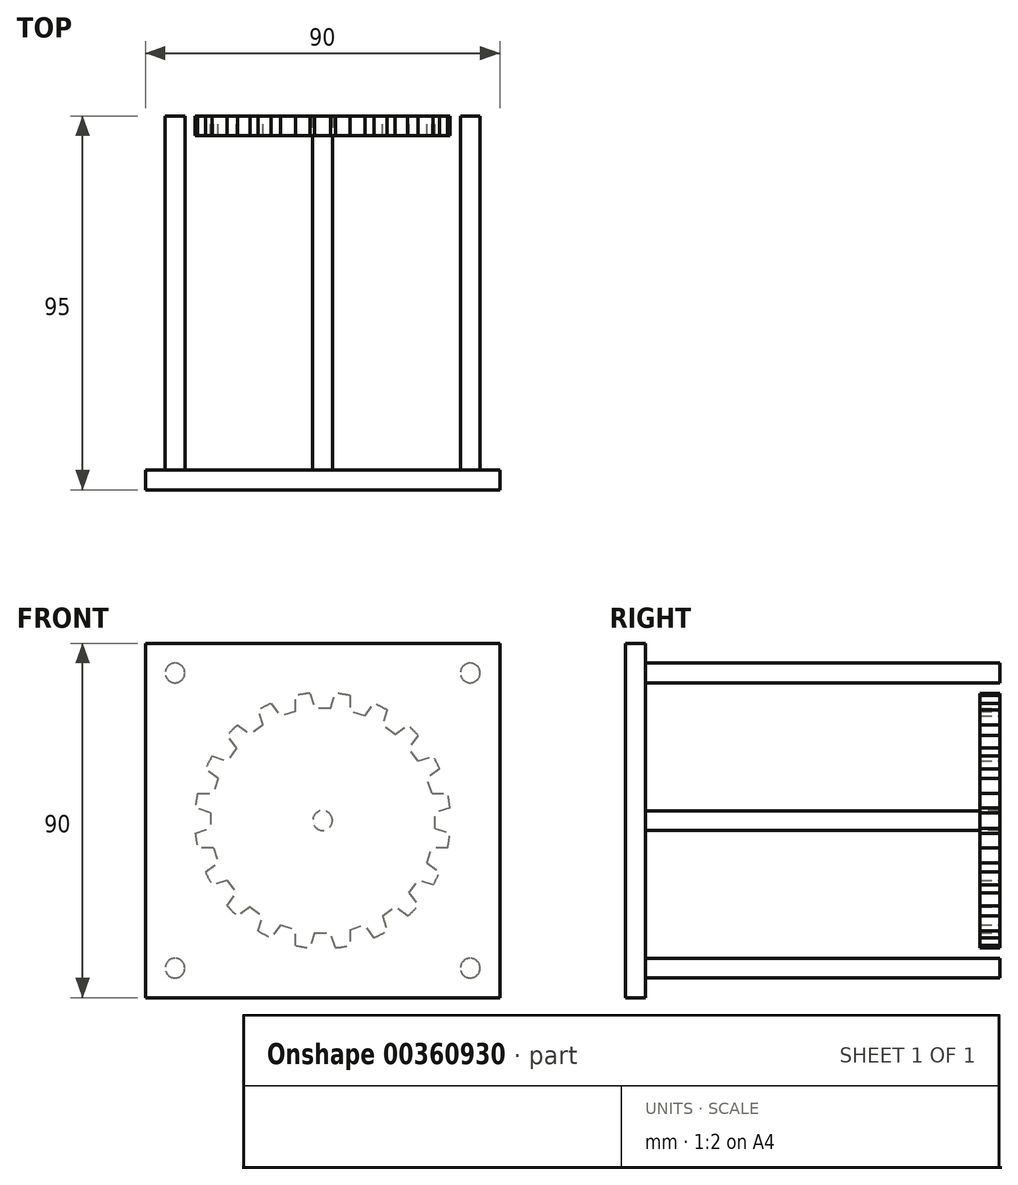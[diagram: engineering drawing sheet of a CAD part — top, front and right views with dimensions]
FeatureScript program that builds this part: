
annotation { "Feature Type Name" : "Feature", "Feature Type Description" : "" }
export const myFeature = defineFeature(function(context is Context, id is Id, definition is map)
    precondition{}
    {
        {
            var Q0;
            Q0=qCreatedBy(makeId("Front.planeOp"),FACE);
            var sketch = newSketch(context, id + "F0", { "sketchPlane" : qUnion([Q0])});
            skLineSegment(sketch, "E0.bottom", {"start": v(45, 45) * mm, "end": v(-45, 45) * mm});
            skLineSegment(sketch, "E0.top", {"start": v(45, -45) * mm, "end": v(-45, -45) * mm});
            skLineSegment(sketch, "E0.left", {"start": v(45, 45) * mm, "end": v(45, -45) * mm});
            skLineSegment(sketch, "E0.right", {"start": v(-45, 45) * mm, "end": v(-45, -45) * mm});
            skSolve(sketch);
        }
        {
            var Q0;
            Q0=makeQuery(id+"F0.imprint","IMPRINT",FACE,{"disambiguationData":[TD([[makeQuery(id+"F0.imprint","IMPRINT",EDGE,{"derivedFrom":sQuery(id+"F0.wireOp",EDGE,"E0.bottom")}),1.0]])]});
            extrude(context, id + "F1", {"entities" : qUnion([Q0]), "depth" : 5 * mm});
        }
        {
            var Q0;
            Q0=makeQuery(id+"F1.opExtrude","CAP_FACE",FACE,{"disambiguationData":[OSD([sQuery(id+"F0.wireOp",EDGE,"E0.bottom"),sQuery(id+"F0.wireOp",EDGE,"E0.top"),sQuery(id+"F0.wireOp",EDGE,"E0.left"),sQuery(id+"F0.wireOp",EDGE,"E0.right")])],"isStart":true});
            var sketch = newSketch(context, id + "F2", { "sketchPlane" : qUnion([Q0])});
            skCircle(sketch, "E1", {"center": v(0, 0) * mm, "radius": 2.5 * mm});
            skSolve(sketch);
        }
        {
            var Q0;
            Q0 = qSketchRegion(id + "F2", true);
            extrude(context, id + "F3", {"entities" : qUnion([Q0]), "operationType" : NewBodyOperationType.ADD, "depth" : 90 * mm});
        }
        {
            var Q0;
            Q0=makeQuery(id+"F1.opExtrude","CAP_FACE",FACE,{"disambiguationData":[OSD([sQuery(id+"F0.wireOp",EDGE,"E0.bottom"),sQuery(id+"F0.wireOp",EDGE,"E0.top"),sQuery(id+"F0.wireOp",EDGE,"E0.left"),sQuery(id+"F0.wireOp",EDGE,"E0.right")])],"isStart":true});
            var sketch = newSketch(context, id + "F4", { "sketchPlane" : qUnion([Q0])});
            skCircle(sketch, "E2", {"center": v(-37.5, 37.5) * mm, "radius": 2.5 * mm});
            skCircle(sketch, "E3", {"center": v(37.5, 37.5) * mm, "radius": 2.5 * mm});
            skCircle(sketch, "E4", {"center": v(37.5, -37.5) * mm, "radius": 2.5 * mm});
            skCircle(sketch, "E5", {"center": v(-37.5, -37.5) * mm, "radius": 2.5 * mm});
            skSolve(sketch);
        }
        {
            var Q0;
            Q0=makeQuery(id+"F4.imprint","IMPRINT",FACE,{"disambiguationData":[TD([[makeQuery(id+"F4.imprint","IMPRINT",EDGE,{"derivedFrom":sQuery(id+"F4.wireOp",EDGE,"E2")}),1.0]])]});
            var Q1;
            Q1=makeQuery(id+"F4.imprint","IMPRINT",FACE,{"disambiguationData":[TD([[makeQuery(id+"F4.imprint","IMPRINT",EDGE,{"derivedFrom":sQuery(id+"F4.wireOp",EDGE,"E3")}),1.0]])]});
            var Q2;
            Q2=makeQuery(id+"F4.imprint","IMPRINT",FACE,{"disambiguationData":[TD([[makeQuery(id+"F4.imprint","IMPRINT",EDGE,{"derivedFrom":sQuery(id+"F4.wireOp",EDGE,"E4")}),1.0]])]});
            var Q3;
            Q3=makeQuery(id+"F4.imprint","IMPRINT",FACE,{"disambiguationData":[TD([[makeQuery(id+"F4.imprint","IMPRINT",EDGE,{"derivedFrom":sQuery(id+"F4.wireOp",EDGE,"E5")}),1.0]])]});
            var Q4;
            Q4=sQuery(id+"F4.wireOp",EDGE,"E2");
            var Q5;
            Q5=sQuery(id+"F4.wireOp",EDGE,"E3");
            var Q6;
            Q6=sQuery(id+"F4.wireOp",EDGE,"E4");
            var Q7;
            Q7=sQuery(id+"F4.wireOp",EDGE,"E5");
            extrude(context, id + "F5", {"entities" : qUnion([Q0, Q1, Q2, Q3]), "operationType" : NewBodyOperationType.ADD, "surfaceEntities" : qUnion([Q4, Q5, Q6, Q7]), "depth" : 90 * mm});
        }
        {
            var Q0;
            Q0=makeQuery(id+"F3.opExtrude","CAP_FACE",FACE,{"disambiguationData":[OSD([sQuery(id+"F2.wireOp",EDGE,"E1")])],"isStart":false});
            var sketch = newSketch(context, id + "F6", { "sketchPlane" : qUnion([Q0])});
            skCircle(sketch, "E6", {"center": v(0, 0) * mm, "radius": 32.5 * mm});
            skSolve(sketch);
        }
        {
            var Q0;
            Q0 = qSketchRegion(id + "F6", true);
            extrude(context, id + "F7", {"entities" : qUnion([Q0]), "oppositeDirection" : true, "depth" : 5 * mm});
        }
        {
            var Q0;
            Q0=makeQuery(id+"F7.opExtrude","CAP_FACE",FACE,{"disambiguationData":[OSD([sQuery(id+"F6.wireOp",EDGE,"E6")])],"isStart":true});
            var sketch = newSketch(context, id + "F8", { "sketchPlane" : qUnion([Q0])});
            skLineSegment(sketch, "E7", {"start": v(0, 32.5) * mm, "end": v(3.24, 32.34) * mm});
            skLineSegment(sketch, "E8", {"start": v(3.24, 32.34) * mm, "end": v(2, 28.53) * mm});
            skLineSegment(sketch, "E9", {"start": v(2, 28.53) * mm, "end": v(0, 28.53) * mm});
            skSolve(sketch);
        }
        {
            var Q0;
            {var subQ0=sQuery(id+"F8.wireOp",EDGE,"E7");Q0=makeQuery(id+"F8.imprint","IMPRINT",FACE,{"disambiguationData":[TD([[makeQuery(id+"F8.imprint","IMPRINT",EDGE,{"derivedFrom":subQ0}),-1.0]])]});}
            var sketch = newSketch(context, id + "F9", { "sketchPlane" : qUnion([Q0])});
            skPoint(sketch, "E10.0", {"position": v(-3.24, 32.34) * mm});
            skPoint(sketch, "E11.0", {"position": v(3.24, 32.34) * mm});
            skArc(sketch, "E12", {"start": v(3.24, 32.34) * mm, "mid": v(0, 33.5) * mm, "end": v(-3.24, 32.34) * mm});
            skPoint(sketch, "E13.0", {"position": v(-2, 28.53) * mm});
            skPoint(sketch, "E14.0", {"position": v(2, 28.53) * mm});
            skLineSegment(sketch, "E15", {"start": v(3.24, 32.34) * mm, "end": v(2, 28.53) * mm});
            skLineSegment(sketch, "E16", {"start": v(-2, 28.53) * mm, "end": v(-3.24, 32.34) * mm});
            skLineSegment(sketch, "E17", {"start": v(-2, 28.53) * mm, "end": v(2, 28.53) * mm});
            skSolve(sketch);
        }
        {
            var Q0;
            Q0 = qSketchRegion(id + "F9", true);
            extrude(context, id + "F10", {"entities" : qUnion([Q0]), "operationType" : NewBodyOperationType.ADD, "depth" : 10 * mm});
        }
        {
            var Q0;
            Q0=makeQuery(id+"F7.opExtrude","SWEPT_BODY",BODY,{"disambiguationData":[OSD([sQuery(id+"F6.wireOp",EDGE,"E6")])]});
            var Q1;
            Q1=makeQuery(id+"F3.opExtrude","CAP_EDGE",EDGE,{"disambiguationData":[OSD([sQuery(id+"F2.wireOp",EDGE,"E1")])],"isStart":false});
            circularPattern(context, id + "F11", {"entities" : qUnion([Q0]), "axis" : qUnion([Q1]), "angle" : 360 * degree, "instanceCount" : 20, "equalSpace" : true});
        }
        {
            var Q0;
            Q0=makeQuery(id+"F11.opPattern","COPY",FACE,{"derivedFrom":makeQuery(id+"F10.opExtrude","CAP_FACE",FACE,{"disambiguationData":[OSD([sQuery(id+"F9.wireOp",EDGE,"E12"),sQuery(id+"F9.wireOp",EDGE,"E15"),sQuery(id+"F9.wireOp",EDGE,"E16"),sQuery(id+"F9.wireOp",EDGE,"E17")])],"isStart":false}),"instanceName":"1"});
            var Q1;
            Q1=makeQuery(id+"F11.opPattern","COPY",FACE,{"derivedFrom":makeQuery(id+"F10.opExtrude","CAP_FACE",FACE,{"disambiguationData":[OSD([sQuery(id+"F9.wireOp",EDGE,"E12"),sQuery(id+"F9.wireOp",EDGE,"E15"),sQuery(id+"F9.wireOp",EDGE,"E16"),sQuery(id+"F9.wireOp",EDGE,"E17")])],"isStart":false}),"instanceName":"2"});
            var Q2;
            Q2=makeQuery(id+"F10.opExtrude","CAP_FACE",FACE,{"disambiguationData":[OSD([sQuery(id+"F9.wireOp",EDGE,"E12"),sQuery(id+"F9.wireOp",EDGE,"E15"),sQuery(id+"F9.wireOp",EDGE,"E16"),sQuery(id+"F9.wireOp",EDGE,"E17")])],"isStart":false});
            var Q3;
            Q3=makeQuery(id+"F11.opPattern","COPY",FACE,{"derivedFrom":makeQuery(id+"F10.opExtrude","CAP_FACE",FACE,{"disambiguationData":[OSD([sQuery(id+"F9.wireOp",EDGE,"E12"),sQuery(id+"F9.wireOp",EDGE,"E15"),sQuery(id+"F9.wireOp",EDGE,"E16"),sQuery(id+"F9.wireOp",EDGE,"E17")])],"isStart":false}),"instanceName":"19"});
            var Q4;
            Q4=makeQuery(id+"F11.opPattern","COPY",FACE,{"derivedFrom":makeQuery(id+"F10.opExtrude","CAP_FACE",FACE,{"disambiguationData":[OSD([sQuery(id+"F9.wireOp",EDGE,"E12"),sQuery(id+"F9.wireOp",EDGE,"E15"),sQuery(id+"F9.wireOp",EDGE,"E16"),sQuery(id+"F9.wireOp",EDGE,"E17")])],"isStart":false}),"instanceName":"18"});
            var Q5;
            Q5=makeQuery(id+"F11.opPattern","COPY",FACE,{"derivedFrom":makeQuery(id+"F10.opExtrude","CAP_FACE",FACE,{"disambiguationData":[OSD([sQuery(id+"F9.wireOp",EDGE,"E12"),sQuery(id+"F9.wireOp",EDGE,"E15"),sQuery(id+"F9.wireOp",EDGE,"E16"),sQuery(id+"F9.wireOp",EDGE,"E17")])],"isStart":false}),"instanceName":"17"});
            var Q6;
            Q6=makeQuery(id+"F11.opPattern","COPY",FACE,{"derivedFrom":makeQuery(id+"F10.opExtrude","CAP_FACE",FACE,{"disambiguationData":[OSD([sQuery(id+"F9.wireOp",EDGE,"E12"),sQuery(id+"F9.wireOp",EDGE,"E15"),sQuery(id+"F9.wireOp",EDGE,"E16"),sQuery(id+"F9.wireOp",EDGE,"E17")])],"isStart":false}),"instanceName":"16"});
            var Q7;
            Q7=makeQuery(id+"F11.opPattern","COPY",FACE,{"derivedFrom":makeQuery(id+"F10.opExtrude","CAP_FACE",FACE,{"disambiguationData":[OSD([sQuery(id+"F9.wireOp",EDGE,"E12"),sQuery(id+"F9.wireOp",EDGE,"E15"),sQuery(id+"F9.wireOp",EDGE,"E16"),sQuery(id+"F9.wireOp",EDGE,"E17")])],"isStart":false}),"instanceName":"15"});
            var Q8;
            Q8=makeQuery(id+"F11.opPattern","COPY",FACE,{"derivedFrom":makeQuery(id+"F10.opExtrude","CAP_FACE",FACE,{"disambiguationData":[OSD([sQuery(id+"F9.wireOp",EDGE,"E12"),sQuery(id+"F9.wireOp",EDGE,"E15"),sQuery(id+"F9.wireOp",EDGE,"E16"),sQuery(id+"F9.wireOp",EDGE,"E17")])],"isStart":false}),"instanceName":"14"});
            var Q9;
            Q9=makeQuery(id+"F11.opPattern","COPY",FACE,{"derivedFrom":makeQuery(id+"F10.opExtrude","CAP_FACE",FACE,{"disambiguationData":[OSD([sQuery(id+"F9.wireOp",EDGE,"E12"),sQuery(id+"F9.wireOp",EDGE,"E15"),sQuery(id+"F9.wireOp",EDGE,"E16"),sQuery(id+"F9.wireOp",EDGE,"E17")])],"isStart":false}),"instanceName":"3"});
            var Q10;
            Q10=makeQuery(id+"F11.opPattern","COPY",FACE,{"derivedFrom":makeQuery(id+"F10.opExtrude","CAP_FACE",FACE,{"disambiguationData":[OSD([sQuery(id+"F9.wireOp",EDGE,"E12"),sQuery(id+"F9.wireOp",EDGE,"E15"),sQuery(id+"F9.wireOp",EDGE,"E16"),sQuery(id+"F9.wireOp",EDGE,"E17")])],"isStart":false}),"instanceName":"4"});
            var Q11;
            Q11=makeQuery(id+"F11.opPattern","COPY",FACE,{"derivedFrom":makeQuery(id+"F10.opExtrude","CAP_FACE",FACE,{"disambiguationData":[OSD([sQuery(id+"F9.wireOp",EDGE,"E12"),sQuery(id+"F9.wireOp",EDGE,"E15"),sQuery(id+"F9.wireOp",EDGE,"E16"),sQuery(id+"F9.wireOp",EDGE,"E17")])],"isStart":false}),"instanceName":"5"});
            var Q12;
            Q12=makeQuery(id+"F11.opPattern","COPY",FACE,{"derivedFrom":makeQuery(id+"F10.opExtrude","CAP_FACE",FACE,{"disambiguationData":[OSD([sQuery(id+"F9.wireOp",EDGE,"E12"),sQuery(id+"F9.wireOp",EDGE,"E15"),sQuery(id+"F9.wireOp",EDGE,"E16"),sQuery(id+"F9.wireOp",EDGE,"E17")])],"isStart":false}),"instanceName":"6"});
            var Q13;
            Q13=makeQuery(id+"F11.opPattern","COPY",FACE,{"derivedFrom":makeQuery(id+"F10.opExtrude","CAP_FACE",FACE,{"disambiguationData":[OSD([sQuery(id+"F9.wireOp",EDGE,"E12"),sQuery(id+"F9.wireOp",EDGE,"E15"),sQuery(id+"F9.wireOp",EDGE,"E16"),sQuery(id+"F9.wireOp",EDGE,"E17")])],"isStart":false}),"instanceName":"7"});
            var Q14;
            Q14=makeQuery(id+"F11.opPattern","COPY",FACE,{"derivedFrom":makeQuery(id+"F10.opExtrude","CAP_FACE",FACE,{"disambiguationData":[OSD([sQuery(id+"F9.wireOp",EDGE,"E12"),sQuery(id+"F9.wireOp",EDGE,"E15"),sQuery(id+"F9.wireOp",EDGE,"E16"),sQuery(id+"F9.wireOp",EDGE,"E17")])],"isStart":false}),"instanceName":"8"});
            var Q15;
            Q15=makeQuery(id+"F11.opPattern","COPY",FACE,{"derivedFrom":makeQuery(id+"F10.opExtrude","CAP_FACE",FACE,{"disambiguationData":[OSD([sQuery(id+"F9.wireOp",EDGE,"E12"),sQuery(id+"F9.wireOp",EDGE,"E15"),sQuery(id+"F9.wireOp",EDGE,"E16"),sQuery(id+"F9.wireOp",EDGE,"E17")])],"isStart":false}),"instanceName":"9"});
            var Q16;
            Q16=makeQuery(id+"F11.opPattern","COPY",FACE,{"derivedFrom":makeQuery(id+"F10.opExtrude","CAP_FACE",FACE,{"disambiguationData":[OSD([sQuery(id+"F9.wireOp",EDGE,"E12"),sQuery(id+"F9.wireOp",EDGE,"E15"),sQuery(id+"F9.wireOp",EDGE,"E16"),sQuery(id+"F9.wireOp",EDGE,"E17")])],"isStart":false}),"instanceName":"10"});
            var Q17;
            Q17=makeQuery(id+"F11.opPattern","COPY",FACE,{"derivedFrom":makeQuery(id+"F10.opExtrude","CAP_FACE",FACE,{"disambiguationData":[OSD([sQuery(id+"F9.wireOp",EDGE,"E12"),sQuery(id+"F9.wireOp",EDGE,"E15"),sQuery(id+"F9.wireOp",EDGE,"E16"),sQuery(id+"F9.wireOp",EDGE,"E17")])],"isStart":false}),"instanceName":"11"});
            var Q18;
            Q18=makeQuery(id+"F11.opPattern","COPY",FACE,{"derivedFrom":makeQuery(id+"F10.opExtrude","CAP_FACE",FACE,{"disambiguationData":[OSD([sQuery(id+"F9.wireOp",EDGE,"E12"),sQuery(id+"F9.wireOp",EDGE,"E15"),sQuery(id+"F9.wireOp",EDGE,"E16"),sQuery(id+"F9.wireOp",EDGE,"E17")])],"isStart":false}),"instanceName":"12"});
            var Q19;
            Q19=makeQuery(id+"F11.opPattern","COPY",FACE,{"derivedFrom":makeQuery(id+"F10.opExtrude","CAP_FACE",FACE,{"disambiguationData":[OSD([sQuery(id+"F9.wireOp",EDGE,"E12"),sQuery(id+"F9.wireOp",EDGE,"E15"),sQuery(id+"F9.wireOp",EDGE,"E16"),sQuery(id+"F9.wireOp",EDGE,"E17")])],"isStart":false}),"instanceName":"13"});
            extrude(context, id + "F12", {"entities" : qUnion([Q0, Q1, Q2, Q3, Q4, Q5, Q6, Q7, Q8, Q9, Q10, Q11, Q12, Q13, Q14, Q15, Q16, Q17, Q18, Q19]), "operationType" : NewBodyOperationType.REMOVE, "oppositeDirection" : true, "depth" : 25 * mm});
        }
    });
